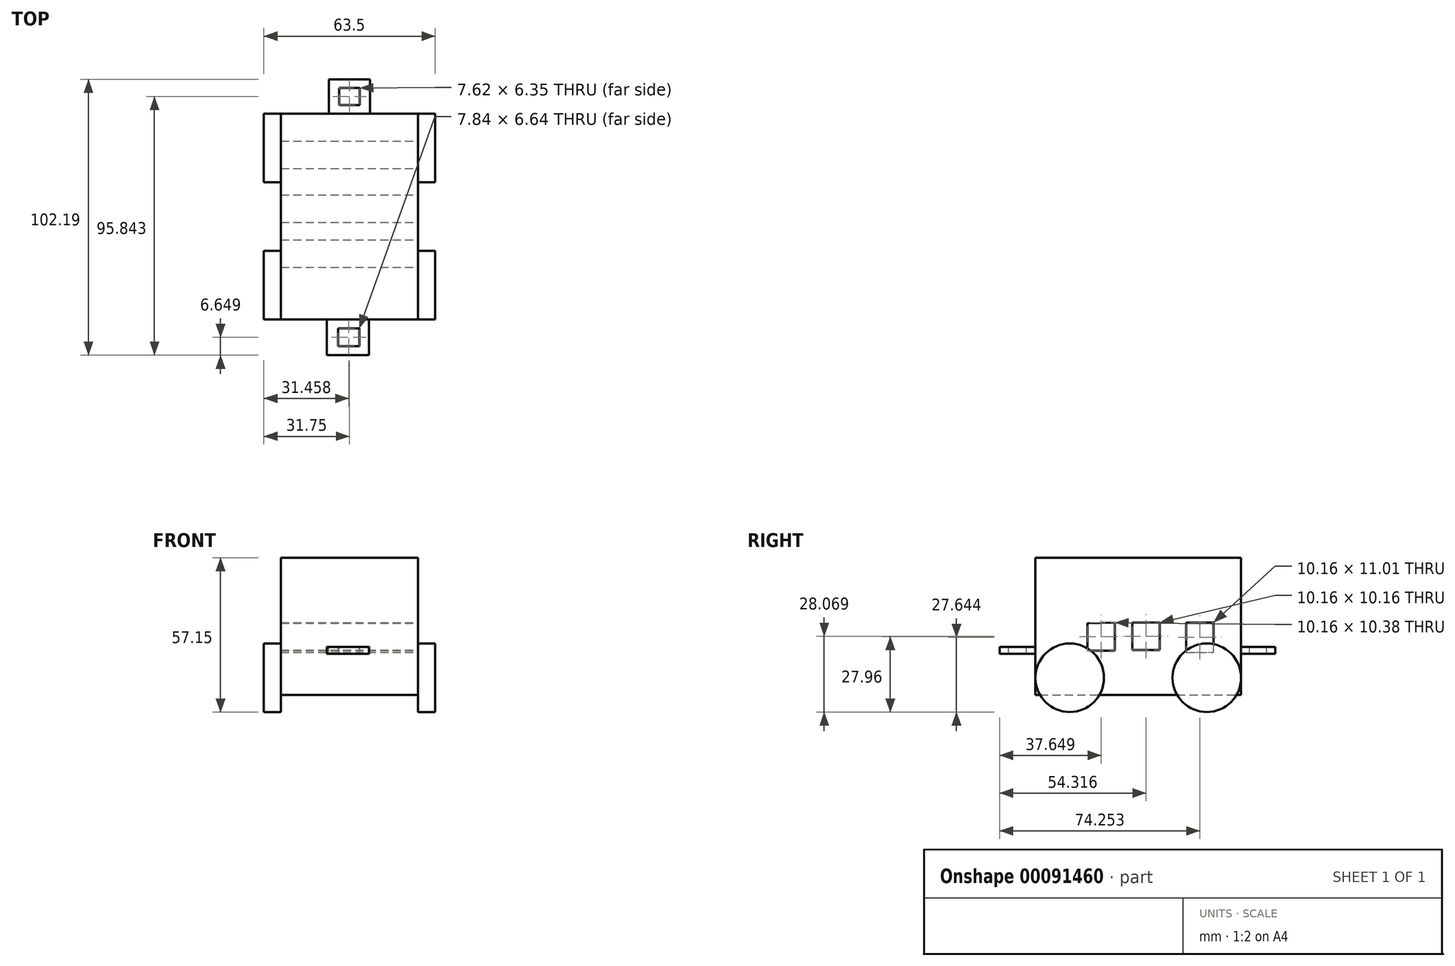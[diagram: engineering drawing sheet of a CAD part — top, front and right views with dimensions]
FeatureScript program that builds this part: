
annotation { "Feature Type Name" : "Feature", "Feature Type Description" : "" }
export const myFeature = defineFeature(function(context is Context, id is Id, definition is map)
    precondition{}
    {
        {
            var Q0;
            Q0=qCreatedBy(makeId("Right.planeOp"),FACE);
            var sketch = newSketch(context, id + "F0", { "sketchPlane" : qUnion([Q0])});
            skLineSegment(sketch, "E0", {"start": v(-19.28, 9.03) * mm, "end": v(56.92, 9.03) * mm});
            skLineSegment(sketch, "E1", {"start": v(56.92, 9.03) * mm, "end": v(56.92, -41.77) * mm});
            skLineSegment(sketch, "E2", {"start": v(-19.28, 9.03) * mm, "end": v(-19.28, -41.77) * mm});
            skLineSegment(sketch, "E3", {"start": v(-19.28, -41.77) * mm, "end": v(56.92, -41.77) * mm});
            skSolve(sketch);
        }
        {
            var Q0;
            Q0 = qSketchRegion(id + "F0", true);
            extrude(context, id + "F1", {"entities" : qUnion([Q0]), "depth" : 50.8 * mm});
        }
        {
            var Q0;
            Q0=makeQuery(id+"F1.opExtrude","CAP_FACE",FACE,{"disambiguationData":[OSD([sQuery(id+"F0.wireOp",EDGE,"E0"),sQuery(id+"F0.wireOp",EDGE,"E1"),sQuery(id+"F0.wireOp",EDGE,"E2"),sQuery(id+"F0.wireOp",EDGE,"E3")])],"isStart":false});
            var sketch = newSketch(context, id + "F2", { "sketchPlane" : qUnion([Q0])});
            skLineSegment(sketch, "E4", {"start": v(0, -15.19) * mm, "end": v(0, -25.35) * mm});
            skLineSegment(sketch, "E5", {"start": v(0, -25.35) * mm, "end": v(10.16, -25.35) * mm});
            skLineSegment(sketch, "E6", {"start": v(10.16, -25.35) * mm, "end": v(10.16, -14.97) * mm});
            skLineSegment(sketch, "E7", {"start": v(0, -15.19) * mm, "end": v(10.16, -14.97) * mm});
            skLineSegment(sketch, "E8", {"start": v(16.67, -14.97) * mm, "end": v(26.83, -14.97) * mm});
            skLineSegment(sketch, "E9", {"start": v(26.83, -14.97) * mm, "end": v(26.83, -25.13) * mm});
            skLineSegment(sketch, "E10", {"start": v(26.83, -25.13) * mm, "end": v(16.67, -25.13) * mm});
            skLineSegment(sketch, "E11", {"start": v(16.67, -25.13) * mm, "end": v(16.67, -14.97) * mm});
            skLineSegment(sketch, "E12", {"start": v(-8.86, -15.19) * mm, "end": v(-8.86, -25.35) * mm});
            skLineSegment(sketch, "E13", {"start": v(-8.86, -25.35) * mm, "end": v(-19.02, -25.35) * mm});
            skLineSegment(sketch, "E14", {"start": v(-19.02, -25.35) * mm, "end": v(-19.02, -15.19) * mm});
            skLineSegment(sketch, "E15", {"start": v(-19.02, -15.19) * mm, "end": v(-8.86, -15.19) * mm});
            skPoint(sketch, "E16.start.orphan", {"position": v(47.54, -14.97) * mm});
            skLineSegment(sketch, "E17", {"start": v(36.6, -14.97) * mm, "end": v(36.6, -25.98) * mm});
            skLineSegment(sketch, "E18", {"start": v(36.6, -25.98) * mm, "end": v(46.76, -25.98) * mm});
            skLineSegment(sketch, "E19", {"start": v(46.76, -25.98) * mm, "end": v(46.76, -14.97) * mm});
            skLineSegment(sketch, "E20", {"start": v(46.76, -14.97) * mm, "end": v(36.6, -14.97) * mm});
            skSolve(sketch);
        }
        {
            var Q0;
            Q0=makeQuery(id+"F2.imprint","IMPRINT",FACE,{"disambiguationData":[TD([[makeQuery(id+"F2.imprint","IMPRINT",EDGE,{"derivedFrom":sQuery(id+"F2.wireOp",EDGE,"E4")}),1.0]])]});
            var Q1;
            Q1=makeQuery(id+"F2.imprint","IMPRINT",FACE,{"disambiguationData":[TD([[makeQuery(id+"F2.imprint","IMPRINT",EDGE,{"derivedFrom":sQuery(id+"F2.wireOp",EDGE,"E8")}),-1.0]])]});
            var Q2;
            Q2=makeQuery(id+"F2.imprint","IMPRINT",FACE,{"disambiguationData":[TD([[makeQuery(id+"F2.imprint","IMPRINT",EDGE,{"derivedFrom":sQuery(id+"F2.wireOp",EDGE,"E17")}),1.0]])]});
            extrude(context, id + "F3", {"entities" : qUnion([Q0, Q1, Q2]), "operationType" : NewBodyOperationType.REMOVE, "oppositeDirection" : true, "depth" : 50.8 * mm});
        }
        {
            var Q0;
            Q0=makeQuery(id+"F1.opExtrude","CAP_FACE",FACE,{"disambiguationData":[OSD([sQuery(id+"F0.wireOp",EDGE,"E0"),sQuery(id+"F0.wireOp",EDGE,"E1"),sQuery(id+"F0.wireOp",EDGE,"E2"),sQuery(id+"F0.wireOp",EDGE,"E3")])],"isStart":true});
            var sketch = newSketch(context, id + "F4", { "sketchPlane" : qUnion([Q0])});
            skCircle(sketch, "E21", {"center": v(-44.22, -35.42) * mm, "radius": 12.7 * mm});
            skCircle(sketch, "E22", {"center": v(6.58, -35.42) * mm, "radius": 12.7 * mm});
            skLineSegment(sketch, "E23", {"start": v(19.28, -16.37) * mm, "end": v(6.58, -35.42) * mm});
            skLineSegment(sketch, "E24", {"start": v(-44.22, -35.42) * mm, "end": v(-56.92, -20.05) * mm});
            skPoint(sketch, "E24.endSnap0", {"position": v(-16.67, -20.05) * mm});
            skLineSegment(sketch, "E25", {"start": v(6.58, -35.42) * mm, "end": v(6.58, 9.03) * mm});
            skLineSegment(sketch, "E26", {"start": v(-44.22, -35.42) * mm, "end": v(-44.22, 9.03) * mm});
            skSolve(sketch);
        }
        {
            var Q0;
            Q0 = qSketchRegion(id + "F4", true);
            extrude(context, id + "F5", {"entities" : qUnion([Q0]), "depth" : 6.35 * mm});
        }
        {
            var Q0;
            Q0=makeQuery(id+"F1.opExtrude","CAP_FACE",FACE,{"disambiguationData":[OSD([sQuery(id+"F0.wireOp",EDGE,"E0"),sQuery(id+"F0.wireOp",EDGE,"E1"),sQuery(id+"F0.wireOp",EDGE,"E2"),sQuery(id+"F0.wireOp",EDGE,"E3")])],"isStart":false});
            var sketch = newSketch(context, id + "F6", { "sketchPlane" : qUnion([Q0])});
            skLineSegment(sketch, "E27", {"start": v(36.6, -25.26) * mm, "end": v(36.6, -25.98) * mm});
            skLineSegment(sketch, "E28", {"start": v(-6.58, -21.37) * mm, "end": v(-6.58, -22.72) * mm});
            skCircle(sketch, "E29", {"center": v(-6.58, -35.42) * mm, "radius": 12.7 * mm});
            skCircle(sketch, "E30", {"center": v(44.22, -35.42) * mm, "radius": 12.7 * mm});
            skLineSegment(sketch, "E31", {"start": v(-6.58, -35.42) * mm, "end": v(-19.28, -16.37) * mm});
            skLineSegment(sketch, "E32", {"start": v(44.22, -35.42) * mm, "end": v(56.92, -16.37) * mm});
            skLineSegment(sketch, "E33", {"start": v(-6.58, -35.42) * mm, "end": v(-6.58, 9.03) * mm});
            skLineSegment(sketch, "E34", {"start": v(44.22, -35.42) * mm, "end": v(44.22, 9.03) * mm});
            skSolve(sketch);
        }
        {
            var Q0;
            Q0 = qSketchRegion(id + "F6", true);
            extrude(context, id + "F7", {"entities" : qUnion([Q0]), "depth" : 6.35 * mm});
        }
        {
            var Q0;
            Q0=makeQuery(id+"F1.opExtrude","SWEPT_FACE",FACE,{"disambiguationData":[OSD([sQuery(id+"F0.wireOp",EDGE,"E0")])]});
            var sketch = newSketch(context, id + "F8", { "sketchPlane" : qUnion([Q0])});
            skLineSegment(sketch, "E35", {"start": v(25.4, 56.92) * mm, "end": v(17.78, 56.92) * mm});
            skLineSegment(sketch, "E36", {"start": v(25.4, 56.92) * mm, "end": v(33.02, 56.92) * mm});
            skLineSegment(sketch, "E37", {"start": v(17.78, 56.92) * mm, "end": v(17.78, 69.62) * mm});
            skLineSegment(sketch, "E38", {"start": v(17.78, 69.62) * mm, "end": v(33.02, 69.62) * mm});
            skLineSegment(sketch, "E39", {"start": v(33.02, 69.62) * mm, "end": v(33.02, 56.92) * mm});
            skLineSegment(sketch, "E40", {"start": v(17.78, 63.27) * mm, "end": v(17.78, 69.62) * mm});
            skLineSegment(sketch, "E41", {"start": v(21.6, 66.45) * mm, "end": v(29.21, 66.45) * mm});
            skPoint(sketch, "E41.startSnap0", {"position": v(21.6, 56.92) * mm});
            skPoint(sketch, "E41.startSnap1", {"position": v(17.78, 66.45) * mm});
            skPoint(sketch, "E41.endSnap0", {"position": v(29.21, 56.92) * mm});
            skPoint(sketch, "E41.endSnap1", {"position": v(17.78, 66.45) * mm});
            skLineSegment(sketch, "E42", {"start": v(17.78, 63.27) * mm, "end": v(17.78, 56.92) * mm});
            skLineSegment(sketch, "E43", {"start": v(21.6, 60.1) * mm, "end": v(29.21, 60.1) * mm});
            skPoint(sketch, "E43.startSnap0", {"position": v(17.78, 60.1) * mm});
            skLineSegment(sketch, "E44", {"start": v(29.21, 60.1) * mm, "end": v(29.21, 66.45) * mm});
            skLineSegment(sketch, "E45", {"start": v(21.6, 66.45) * mm, "end": v(21.6, 60.1) * mm});
            skLineSegment(sketch, "E46", {"start": v(25.4, -19.28) * mm, "end": v(32.66, -19.28) * mm});
            skLineSegment(sketch, "E47", {"start": v(32.66, -19.28) * mm, "end": v(32.66, -32.57) * mm});
            skLineSegment(sketch, "E48", {"start": v(32.66, -32.57) * mm, "end": v(16.97, -32.57) * mm});
            skLineSegment(sketch, "E49", {"start": v(16.97, -32.57) * mm, "end": v(16.97, -19.28) * mm});
            skLineSegment(sketch, "E50", {"start": v(16.97, -19.28) * mm, "end": v(25.4, -19.28) * mm});
            skLineSegment(sketch, "E51", {"start": v(32.66, -25.92) * mm, "end": v(32.66, -19.28) * mm});
            skLineSegment(sketch, "E52", {"start": v(32.66, -25.92) * mm, "end": v(32.66, -32.57) * mm});
            skLineSegment(sketch, "E53", {"start": v(29.03, -29.24) * mm, "end": v(21.19, -29.24) * mm});
            skPoint(sketch, "E53.startSnap0", {"position": v(29.03, -19.28) * mm});
            skPoint(sketch, "E53.startSnap1", {"position": v(32.66, -29.24) * mm});
            skPoint(sketch, "E53.endSnap0", {"position": v(21.19, -19.28) * mm});
            skLineSegment(sketch, "E54", {"start": v(21.19, -29.24) * mm, "end": v(21.19, -22.6) * mm});
            skPoint(sketch, "E54.endSnap0", {"position": v(32.66, -22.6) * mm});
            skLineSegment(sketch, "E55", {"start": v(21.19, -22.6) * mm, "end": v(29.03, -22.6) * mm});
            skLineSegment(sketch, "E56", {"start": v(29.03, -22.6) * mm, "end": v(29.03, -29.24) * mm});
            skSolve(sketch);
        }
        {
            var Q0;
            Q0 = qSketchRegion(id + "F8", true);
            extrude(context, id + "F9", {"entities" : qUnion([Q0]), "operationType" : NewBodyOperationType.ADD, "oppositeDirection" : true, "depth" : 35.56 * mm});
        }
        {
            var Q0;
            Q0 = qSketchRegion(id + "F8", true);
            extrude(context, id + "F10", {"entities" : qUnion([Q0]), "operationType" : NewBodyOperationType.REMOVE, "oppositeDirection" : true, "depth" : 33.02 * mm});
        }
    });
